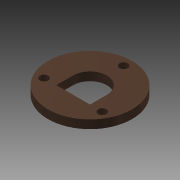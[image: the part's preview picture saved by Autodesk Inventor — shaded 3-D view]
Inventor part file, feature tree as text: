
AUTODESK INVENTOR PART (.ipt)
format: ipt  version: 2015 (Build 190159000, 159)  size: 98,304 bytes
history: native  units: mm
features: extrude x3, sketch x3
ambient origin geometry x8: Origin, YZ Plane, XZ Plane, XY Plane, X Axis, Y Axis, Z Axis, Center Point
bodies: 实体1 (feature_tree)
feature tree (6):
  extrude  "拉伸1"  Depth=5.0mm TaperAngle=0.0deg
  extrude  "拉伸2"  Depth=5.0mm TaperAngle=0.0deg
  extrude  "拉伸3"  Depth=5.0mm
  sketch  "草图1"  dims[d0=50.0mm d1=5.0mm d2=0.0mm]
  sketch  "草图2"  dims[d3=20.0mm d4=5.0mm d5=0.0mm]
  sketch  "草图3"  dims[d6=5.0mm d7=5.0mm d8=5.0mm d9=20.0mm d10=120.0deg d11=120.0deg d12=5.0mm d13=0.0mm]
